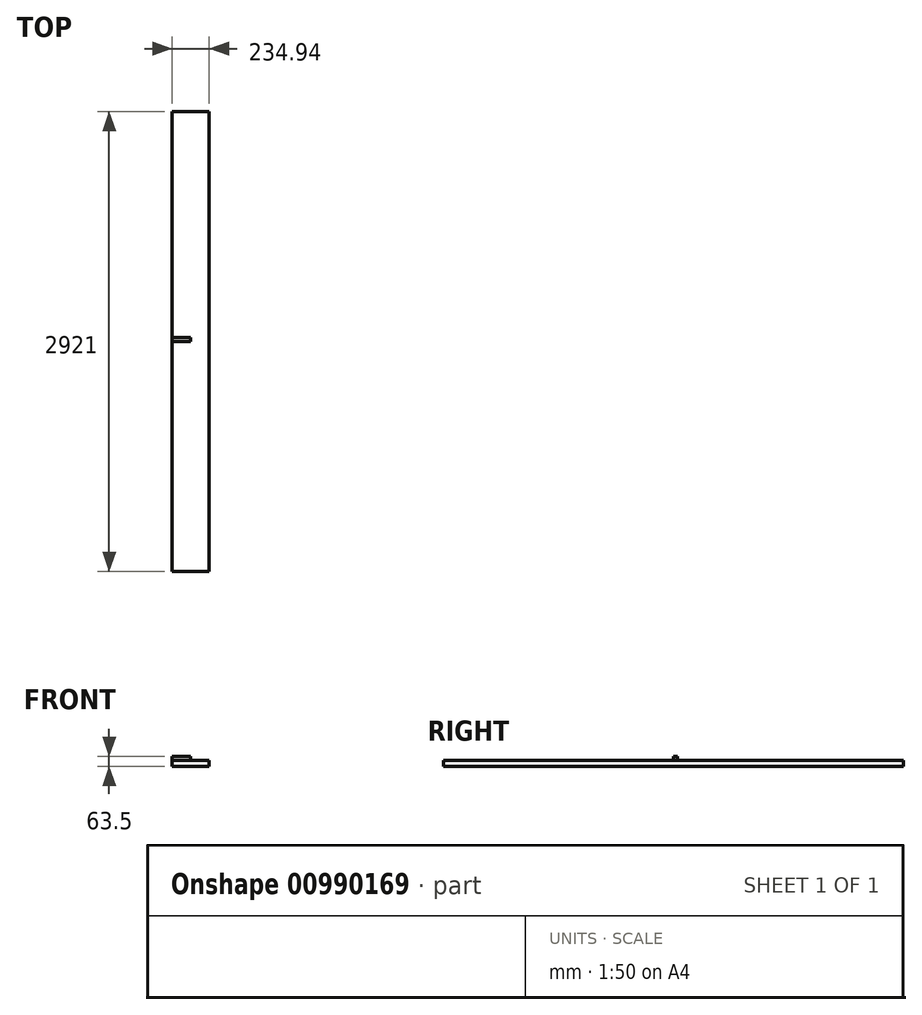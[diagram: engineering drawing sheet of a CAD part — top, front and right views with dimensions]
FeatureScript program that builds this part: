
annotation { "Feature Type Name" : "Feature", "Feature Type Description" : "" }
export const myFeature = defineFeature(function(context is Context, id is Id, definition is map)
    precondition{}
    {
        {
            assignVariable(context, id + "F0", {"name" : "w", "anyValue" : 38.1 * mm});
        }
        {
            var Q0;
            Q0=qCreatedBy(makeId("Top.planeOp"),FACE);
            var sketch = newSketch(context, id + "F1", { "sketchPlane" : qUnion([Q0])});
            skLineSegment(sketch, "E0.bottom", {"start": v(117.47, 1460.5) * mm, "end": v(-117.48, 1460.5) * mm});
            skLineSegment(sketch, "E0.top", {"start": v(117.47, -1460.5) * mm, "end": v(-117.48, -1460.5) * mm});
            skLineSegment(sketch, "E0.left", {"start": v(117.47, 1460.5) * mm, "end": v(117.47, -1460.5) * mm});
            skLineSegment(sketch, "E0.right", {"start": v(-117.48, 1460.5) * mm, "end": v(-117.48, -1460.5) * mm});
            skPoint(sketch, "E0.middle", {"position": v(0, 0) * mm});
            skSolve(sketch);
        }
        {
            var Q0;
            Q0=qSketchRegion(id+"F1",true);
            extrude(context, id + "F2", {"entities" : qUnion([Q0]), "depth" : getVariable(context, 'w'), "offsetDistance" : 25.4 * mm});
        }
        {
            var Q0;
            Q0=makeQuery(id+"F2.opExtrude","CAP_FACE",FACE,{"disambiguationData":[OSD([sQuery(id+"F1.wireOp",EDGE,"E0.bottom"),sQuery(id+"F1.wireOp",EDGE,"E0.top"),sQuery(id+"F1.wireOp",EDGE,"E0.left"),sQuery(id+"F1.wireOp",EDGE,"E0.right")])],"isStart":false});
            var sketch = newSketch(context, id + "F3", { "sketchPlane" : qUnion([Q0])});
            skLineSegment(sketch, "E1.bottom", {"start": v(0, 0) * mm, "end": v(-117.48, 0) * mm});
            skLineSegment(sketch, "E1.top", {"start": v(0, 24.76) * mm, "end": v(-117.48, 24.76) * mm});
            skLineSegment(sketch, "E1.left", {"start": v(0, 0) * mm, "end": v(0, 24.76) * mm});
            skLineSegment(sketch, "E1.right", {"start": v(-117.48, 0) * mm, "end": v(-117.48, 24.76) * mm});
            skSolve(sketch);
        }
        {
            var Q0;
            Q0 = qSketchRegion(id + "F3", true);
            extrude(context, id + "F4", {"entities" : qUnion([Q0]), "operationType" : NewBodyOperationType.ADD, "depth" : 25.4 * mm, "offsetDistance" : 25.4 * mm});
        }
    });
